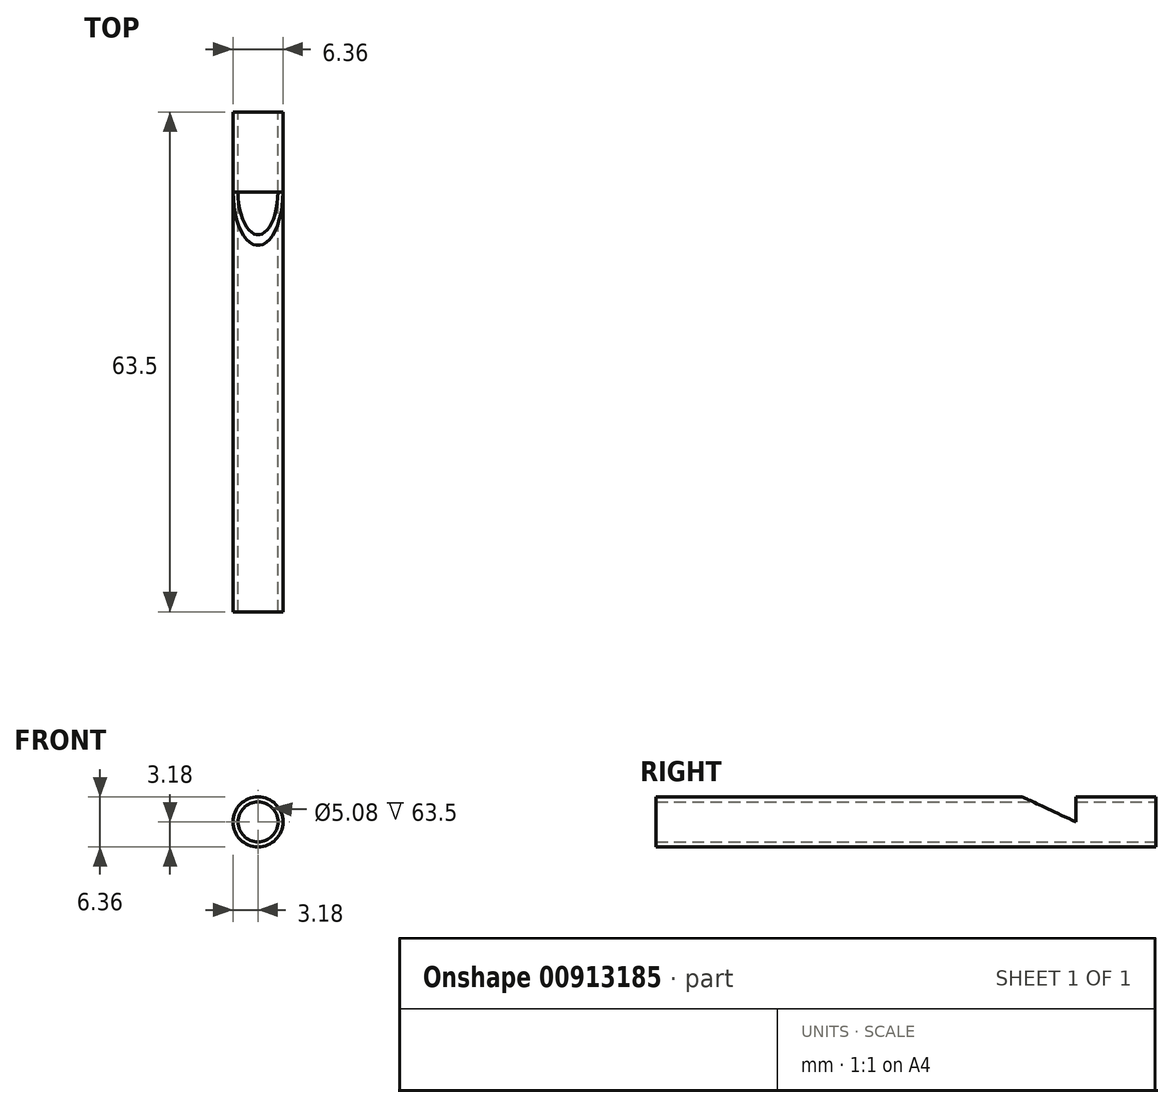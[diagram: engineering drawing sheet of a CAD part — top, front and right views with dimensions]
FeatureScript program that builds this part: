
annotation { "Feature Type Name" : "Feature", "Feature Type Description" : "" }
export const myFeature = defineFeature(function(context is Context, id is Id, definition is map)
    precondition{}
    {
        {
            var Q0;
            Q0=qCreatedBy(makeId("Front.planeOp"),FACE);
            var sketch = newSketch(context, id + "F0", { "sketchPlane" : qUnion([Q0])});
            skCircle(sketch, "E0", {"center": v(0, 0) * mm, "radius": 2.54 * mm});
            skCircle(sketch, "E1", {"center": v(0, 0) * mm, "radius": 3.18 * mm});
            skSolve(sketch);
        }
        {
            var Q0;
            Q0 = qSketchRegion(id + "F0", true);
            extrude(context, id + "F1", {"entities" : qUnion([Q0]), "depth" : 63.5 * mm, "offsetDistance" : 25.4 * mm});
        }
        {
            var Q0;
            Q0=qCreatedBy(makeId("Right.planeOp"),FACE);
            var sketch = newSketch(context, id + "F2", { "sketchPlane" : qUnion([Q0])});
            skLineSegment(sketch, "E2", {"start": v(-10.16, 0) * mm, "end": v(-10.16, 3.55) * mm});
            skLineSegment(sketch, "E3", {"start": v(-10.16, 3.55) * mm, "end": v(-17.78, 3.55) * mm});
            skLineSegment(sketch, "E4", {"start": v(-17.78, 3.55) * mm, "end": v(-10.16, 0) * mm});
            skSolve(sketch);
        }
        {
            var Q0;
            Q0 = qSketchRegion(id + "F2", true);
            extrude(context, id + "F3", {"entities" : qUnion([Q0]), "operationType" : NewBodyOperationType.REMOVE, "endBound" : BoundingType.THROUGH_ALL, "depth" : 25.4 * mm, "offsetDistance" : 25.4 * mm, "hasSecondDirection" : true, "secondDirectionOppositeDirection" : true, "secondDirectionDepth" : 50.8 * mm});
        }
    });
